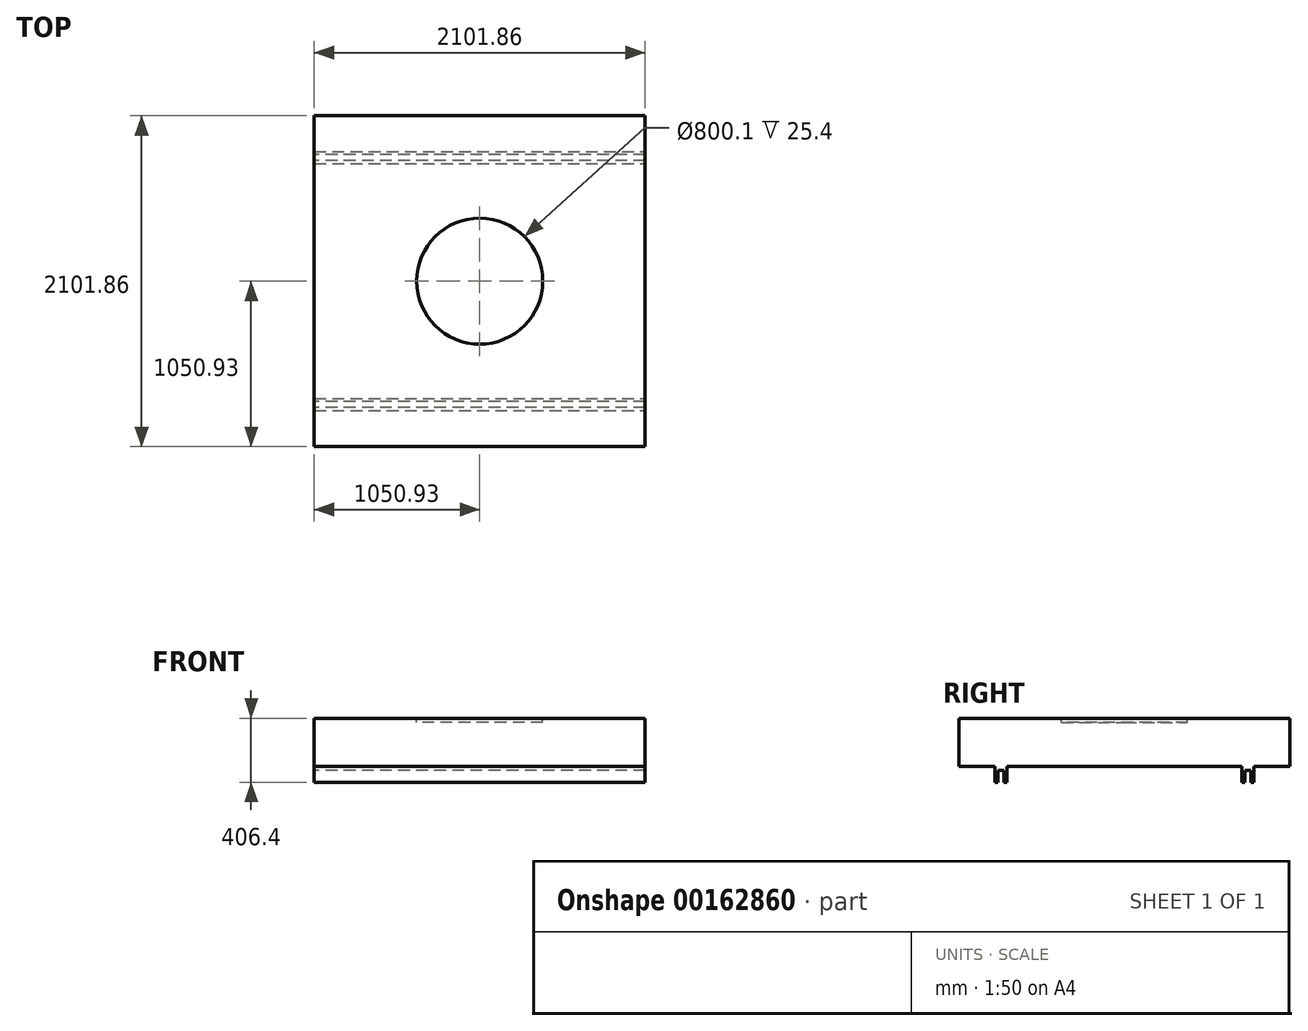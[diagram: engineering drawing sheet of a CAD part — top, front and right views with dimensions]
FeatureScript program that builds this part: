
annotation { "Feature Type Name" : "Feature", "Feature Type Description" : "" }
export const myFeature = defineFeature(function(context is Context, id is Id, definition is map)
    precondition{}
    {
        {
            var Q0;
            Q0=qCreatedBy(makeId("Top.planeOp"),FACE);
            var sketch = newSketch(context, id + "F0", { "sketchPlane" : qUnion([Q0])});
            skLineSegment(sketch, "E0.bottom", {"start": v(1050.93, -1050.92) * mm, "end": v(-1050.93, -1050.93) * mm});
            skLineSegment(sketch, "E0.top", {"start": v(1050.93, 1050.93) * mm, "end": v(-1050.93, 1050.92) * mm});
            skLineSegment(sketch, "E0.left", {"start": v(1050.93, -1050.92) * mm, "end": v(1050.93, 1050.93) * mm});
            skLineSegment(sketch, "E0.right", {"start": v(-1050.93, -1050.93) * mm, "end": v(-1050.93, 1050.92) * mm});
            skPoint(sketch, "E0.middle", {"position": v(0, 0) * mm});
            skSolve(sketch);
        }
        {
            var Q0;
            Q0 = qSketchRegion(id + "F0", true);
            extrude(context, id + "F1", {"entities" : qUnion([Q0]), "depth" : 304.8 * mm});
        }
        {
            var Q0;
            Q0=makeQuery(id+"F1.opExtrude","CAP_FACE",FACE,{"disambiguationData":[OSD([sQuery(id+"F0.wireOp",EDGE,"E0.bottom"),sQuery(id+"F0.wireOp",EDGE,"E0.top"),sQuery(id+"F0.wireOp",EDGE,"E0.left"),sQuery(id+"F0.wireOp",EDGE,"E0.right")])],"isStart":false});
            var sketch = newSketch(context, id + "F2", { "sketchPlane" : qUnion([Q0])});
            skCircle(sketch, "E1", {"center": v(0, 0) * mm, "radius": 400.05 * mm});
            skSolve(sketch);
        }
        {
            var Q0;
            Q0 = qSketchRegion(id + "F2", true);
            extrude(context, id + "F3", {"entities" : qUnion([Q0]), "operationType" : NewBodyOperationType.REMOVE, "oppositeDirection" : true, "depth" : 25.4 * mm});
        }
        {
            var Q0;
            Q0=makeQuery(id+"F1.opExtrude","CAP_FACE",FACE,{"disambiguationData":[OSD([sQuery(id+"F0.wireOp",EDGE,"E0.bottom"),sQuery(id+"F0.wireOp",EDGE,"E0.top"),sQuery(id+"F0.wireOp",EDGE,"E0.left"),sQuery(id+"F0.wireOp",EDGE,"E0.right")])],"isStart":true});
            var sketch = newSketch(context, id + "F4", { "sketchPlane" : qUnion([Q0])});
            skLineSegment(sketch, "E2.bottom", {"start": v(-1050.93, 822.32) * mm, "end": v(1050.93, 822.32) * mm});
            skLineSegment(sketch, "E2.top", {"start": v(-1050.93, 746.12) * mm, "end": v(1050.93, 746.12) * mm});
            skLineSegment(sketch, "E2.left", {"start": v(-1050.93, 822.32) * mm, "end": v(-1050.93, 746.12) * mm});
            skLineSegment(sketch, "E2.right", {"start": v(1050.93, 822.32) * mm, "end": v(1050.93, 746.12) * mm});
            skLineSegment(sketch, "E3.bottom", {"start": v(-1050.93, -746.13) * mm, "end": v(1050.93, -746.13) * mm});
            skLineSegment(sketch, "E3.top", {"start": v(-1050.93, -822.33) * mm, "end": v(1050.93, -822.33) * mm});
            skLineSegment(sketch, "E3.left", {"start": v(-1050.93, -746.13) * mm, "end": v(-1050.93, -822.33) * mm});
            skLineSegment(sketch, "E3.right", {"start": v(1050.93, -746.13) * mm, "end": v(1050.93, -822.33) * mm});
            skSolve(sketch);
        }
        {
            var Q0;
            Q0 = qSketchRegion(id + "F4", true);
            extrude(context, id + "F5", {"entities" : qUnion([Q0]), "operationType" : NewBodyOperationType.ADD, "depth" : 101.6 * mm});
        }
        {
            var Q0;
            Q0=makeQuery(id+"F5.boolean.opBoolean","MERGE",FACE,{"derivedFrom":[makeQuery(id+"F1.opExtrude","SWEPT_FACE",FACE,{"disambiguationData":[OSD([sQuery(id+"F0.wireOp",EDGE,"E0.right")])]}),makeQuery(id+"F5.opExtrude","SWEPT_FACE",FACE,{"disambiguationData":[OSD([sQuery(id+"F4.wireOp",EDGE,"E2.left")])]}),makeQuery(id+"F5.opExtrude","SWEPT_FACE",FACE,{"disambiguationData":[OSD([sQuery(id+"F4.wireOp",EDGE,"E3.left")])]})]});
            var sketch = newSketch(context, id + "F6", { "sketchPlane" : qUnion([Q0])});
            skLineSegment(sketch, "E4.top", {"start": v(-765.17, -25.4) * mm, "end": v(-803.27, -25.4) * mm});
            skLineSegment(sketch, "E4.left", {"start": v(-765.17, -101.6) * mm, "end": v(-765.17, -25.4) * mm});
            skLineSegment(sketch, "E4.right", {"start": v(-803.27, -101.6) * mm, "end": v(-803.27, -25.4) * mm});
            skPoint(sketch, "E4.middle", {"position": v(-784.22, -101.6) * mm});
            skLineSegment(sketch, "E5", {"start": v(-803.27, -101.6) * mm, "end": v(-765.17, -101.6) * mm});
            skPoint(sketch, "E4.bottom.end.orphan", {"position": v(-803.27, -177.8) * mm});
            skPoint(sketch, "E6.orphan", {"position": v(-765.17, -177.8) * mm});
            skLineSegment(sketch, "E7.top", {"start": v(803.27, -25.4) * mm, "end": v(765.17, -25.4) * mm});
            skLineSegment(sketch, "E7.left", {"start": v(803.27, -101.6) * mm, "end": v(803.27, -25.4) * mm});
            skLineSegment(sketch, "E7.right", {"start": v(765.17, -101.6) * mm, "end": v(765.17, -25.4) * mm});
            skPoint(sketch, "E7.middle", {"position": v(784.22, -101.6) * mm});
            skLineSegment(sketch, "E8", {"start": v(765.17, -101.6) * mm, "end": v(803.27, -101.6) * mm});
            skPoint(sketch, "E7.bottom.end.orphan", {"position": v(765.17, -177.8) * mm});
            skPoint(sketch, "E7.bottom.start.orphan", {"position": v(803.27, -177.8) * mm});
            skSolve(sketch);
        }
        {
            var Q0;
            Q0 = qSketchRegion(id + "F6", true);
            extrude(context, id + "F7", {"entities" : qUnion([Q0]), "operationType" : NewBodyOperationType.REMOVE, "endBound" : BoundingType.THROUGH_ALL, "oppositeDirection" : true, "depth" : 25.4 * mm});
        }
    });
